# Revit family: Domotics-CablaggioStrutturato-GEWISS-QUADRI_PARETE_10_6U
name_source: partatom
category: Apparecchi elettrici
units: mm (PartAtom-declared; Revit-internal decimal feet)

## family parameters
Condiviso = No
Host = Superficie
Mantenere orientamento annotazione = Sì
Punto di calcolo locali = Sì
Quota connettore circolare = Usa diametro
Taglio con vuoti quando caricato = No
Tipo di parte = Normale

## types (1)
- Domotics-CablaggioStrutturato-GEWISS-QUADRI_PARETE_10_6U
    Apertura porta = 180°
    Catalogo = DOMOTICS
    Categoria = Quadro da parete 10"
    Codice Electrocod = 3752
    Colore = Grigio (RAL 7035)
    Descrizione = QUADRO DA PARETE 10 8U P=265MM
    Dim. esterne BxHxP (mm) = 325x400x262
    Finitura = Bucciata
    Grado di protezione = IP20
    IDF = 5ac9469c-4090-481c-b30f-03194449df13
    IDT = 6908dd95ba2d4d7d80b407934de9d0a7
    Immagine tipo = A.jpg
    Materiale = Acciaio
    Modello = GW38432
    N. montanti = 2
    Portata statica = 15KG
    Produttore = GEWISS S.p.A.
    Prospetto di default = 1219 mm
    SEO = Quadro
    Scheda Tecnica = https://www.gewiss.com
    Tipologia porta = Reversibile
    URL = https://www.gewiss.com
    Unità di cablaggio = 8 U
    Versione file RFA = 21.2

## geometry (parser evidence)
native form markers: Sweep x3
no freeform markers — native parametric forms only
